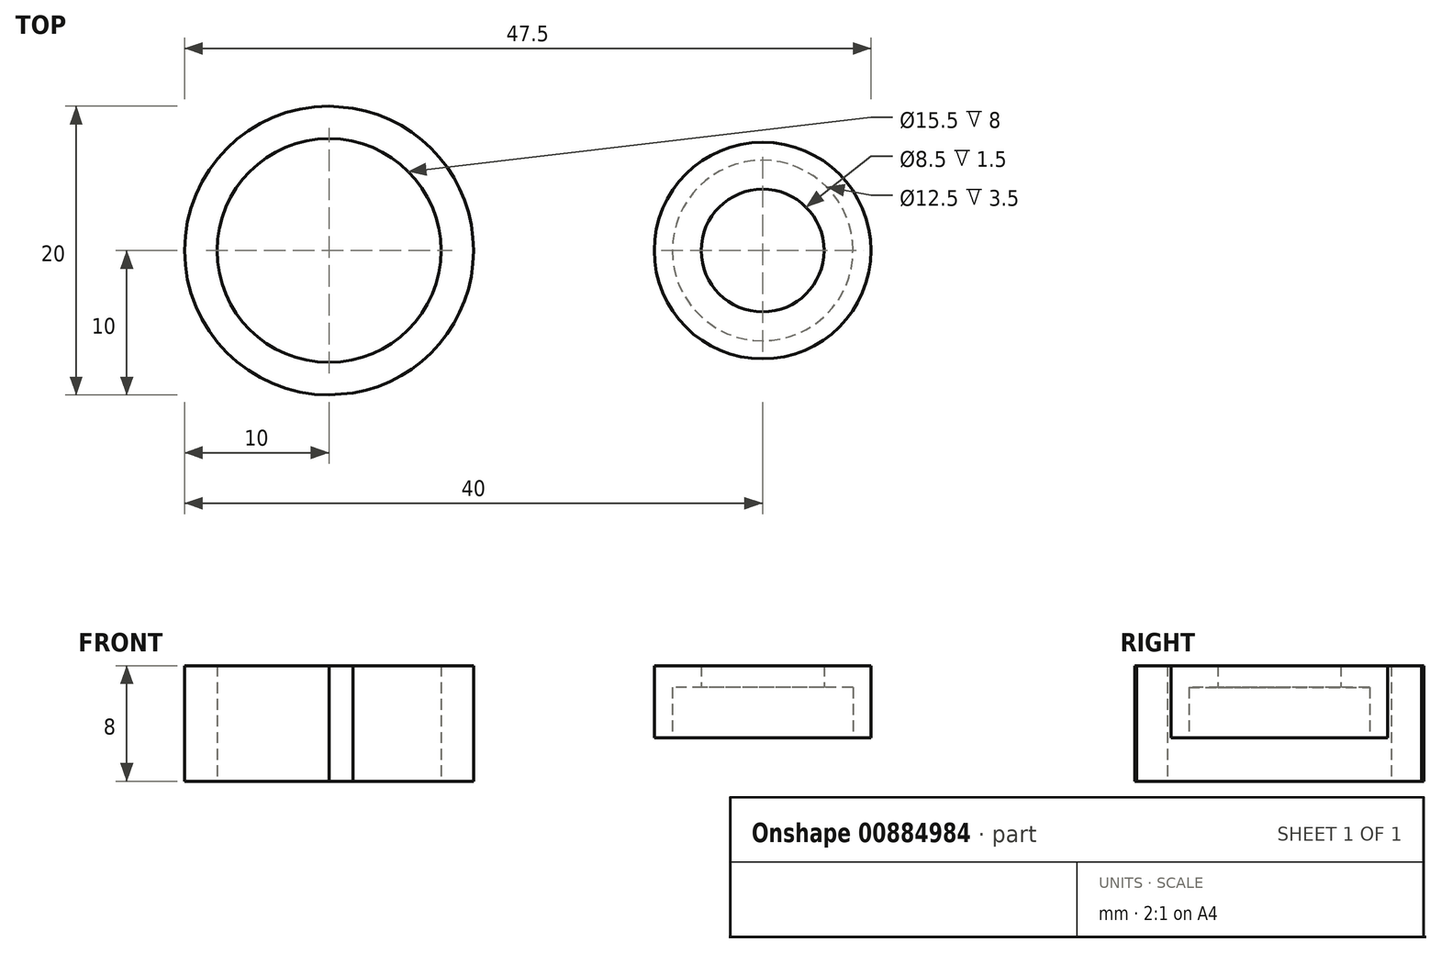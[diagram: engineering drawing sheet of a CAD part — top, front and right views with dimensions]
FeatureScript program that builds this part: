
annotation { "Feature Type Name" : "Feature", "Feature Type Description" : "" }
export const myFeature = defineFeature(function(context is Context, id is Id, definition is map)
    precondition{}
    {
        {
            var Q0;
            Q0=qCreatedBy(makeId("Top.planeOp"),FACE);
            var sketch = newSketch(context, id + "F0", { "sketchPlane" : qUnion([Q0])});
            skCircle(sketch, "E0", {"center": v(0, 0) * mm, "radius": 7.75 * mm});
            skCircle(sketch, "E1", {"center": v(0, 0) * mm, "radius": 10 * mm});
            skLineSegment(sketch, "E2", {"start": v(0, 0) * mm, "end": v(30, 0) * mm, "construction": true});
            skCircle(sketch, "E3", {"center": v(30, 0) * mm, "radius": 7.5 * mm});
            skLineSegment(sketch, "E4", {"start": v(0, 10) * mm, "end": v(30, 7.5) * mm});
            skLineSegment(sketch, "E5", {"start": v(0, -10) * mm, "end": v(30, -7.5) * mm});
            skCircle(sketch, "E6", {"center": v(30, 0) * mm, "radius": 4.25 * mm});
            skCircle(sketch, "E7", {"center": v(30, 0) * mm, "radius": 6.25 * mm});
            skSolve(sketch);
        }
        {
            var Q0;
            Q0=makeQuery(id+"F0.imprint","IMPRINT",FACE,{"disambiguationData":[TD([[makeQuery(id+"F0.imprint","IMPRINT",EDGE,{"derivedFrom":sQuery(id+"F0.wireOp",EDGE,"E0")}),-1.0]])]});
            var Q1;
            {var subQ0=sQuery(id+"F0.wireOp",EDGE,"E4");var subQ1=sQuery(id+"F0.wireOp",EDGE,"E1");var subQ2=makeQuery(id+"F0.imprint","INTERSECT",VERTEX,{"disambiguationData":[OD(1.0)],"derivedFrom":[subQ1,subQ0]});Q1=makeQuery(id+"F0.imprint","IMPRINT",FACE,{"disambiguationData":[TD([[makeQuery(id+"F0.imprint","IMPRINT",EDGE,{"disambiguationData":[TD([[subQ2,1.0]])],"derivedFrom":subQ1}),-1.0]])]});}
            var Q2;
            Q2=makeQuery(id+"F0.imprint","IMPRINT",FACE,{"disambiguationData":[TD([[makeQuery(id+"F0.imprint","IMPRINT",EDGE,{"derivedFrom":sQuery(id+"F0.wireOp",EDGE,"E6")}),-1.0]])]});
            var Q3;
            Q3=makeQuery(id+"F0.imprint","IMPRINT",FACE,{"disambiguationData":[TD([[makeQuery(id+"F0.imprint","IMPRINT",EDGE,{"derivedFrom":sQuery(id+"F0.wireOp",EDGE,"E7")}),-1.0]])]});
            extrude(context, id + "F1", {"entities" : qUnion([Q0, Q1, Q2, Q3]), "depth" : 5 * mm, "offsetDistance" : 25 * mm});
        }
        {
            var Q0;
            Q0=makeQuery(id+"F0.imprint","IMPRINT",FACE,{"disambiguationData":[TD([[makeQuery(id+"F0.imprint","IMPRINT",EDGE,{"derivedFrom":sQuery(id+"F0.wireOp",EDGE,"E0")}),-1.0]])]});
            extrude(context, id + "F2", {"entities" : qUnion([Q0]), "operationType" : NewBodyOperationType.ADD, "oppositeDirection" : true, "depth" : 3 * mm, "offsetDistance" : 25 * mm});
        }
        {
            var Q0;
            Q0=makeQuery(id+"F0.imprint","IMPRINT",FACE,{"disambiguationData":[TD([[makeQuery(id+"F0.imprint","IMPRINT",EDGE,{"derivedFrom":sQuery(id+"F0.wireOp",EDGE,"E6")}),-1.0]])]});
            extrude(context, id + "F3", {"entities" : qUnion([Q0]), "operationType" : NewBodyOperationType.REMOVE, "depth" : 3.5 * mm, "offsetDistance" : 25 * mm});
        }
    });
